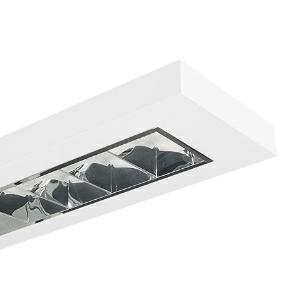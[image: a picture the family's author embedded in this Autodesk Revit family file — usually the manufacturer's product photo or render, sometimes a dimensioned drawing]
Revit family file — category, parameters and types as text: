
# Revit family: 3f_filippi_-_3f_travetta_di_2mg_3f_filippi_-_11597_-_3f_trav__led_di_2x22w-940_dali_2mg_l1590_0594
name_source: partatom
category: Lighting Fixtures
units: mm (PartAtom-declared; Revit-internal decimal feet)

## family parameters
Cut with Voids When Loaded = No
Host = Face
Light Source = No
Part Type = Normal
Room Calculation Point = No
Round Connector Dimension = Use Diameter
Shared = No

## types (1)
- 3F Filippi - 3F Travetta DI 2MG (1 x LED, 4545 lm, 49 W, 4000 K)
    Apparent Load = 49 VA
    Approval mark = ENEC
    CIE Flux Codes = 61 98 100 85 100
    Color Rendering = 90
    Color Temperature = 4000 K
    Control Gear = Electronic transformer
    Default Elevation = 1800 mm
    Description = ILLUMINOTECHNICAL
Luminous efficiency 100% (DLOR 85%, ULOR 15%).
Initial luminous flux of the luminaire 4545 lm.
Symmetric direct-indirect distribution.
Installation Interdistance Transv.D = 2.02 x hu - Long.D = 1.27 x hu.
Average luminance <1000 cd/m² for radial angles >65°.
Tabular UGR (CIE 117 - 4H-8H; S=0.25H; 70/50/20): RUG 17.5 - 16.9.
Beam angle: 99° - 72°.
Luminous efficacy 93 lm/W.
Lifetime (L93/B10): 30000 h. (tq+25°C)
Lifetime (L90/B10): 50000 h. (tq+25°C)
Lifetime (L85/B10): 80000 h. (tq+25°C)
Lifetime (L80/B10): 100000 h. (tq+25°C)
Sudden decreased luminous flux after 50000 hours: 0% (C0).
Photobiological safety in compliance with IEC/TR 62778: RG0 risk exempt, (IEC 62471).
In compliance with IEC/EN 62722-2-1 - IEC/EN 62717 standards.

SOURCE
2 linear LED modules 22W/940.
Energy efficiency class (UE 2019/2020 - UE 2019/2015): E.
CIE 13.3 Colour rendering index: CRI >90 (R9 >50%).
IES TM-30 Fidelity Index: Rf = 92 Rg = 101.
CCT nominal colour temperature 4000 K.
Colour initial tolerance (MacAdam): SDCM 2.

MECHANICAL
Housing with squared shape in white painted galvannealed steel, with nonreflecting surface.
2MG parabolic louvre, high efficiency, in specular aluminium with superficial titanium-magnesium treatment, non-iridescent, with transverse blades closed at the top.
Prismatic flat diffuser in transparent methacrylate (PMMA), multilenticular, anti-glare, prismatic exterior, placed above louvre blades.
Film protective against dust and finger marks, adhesive, attached to louvre.
Upper holes closing film made of opal polycarbonate.
Luminaire with limited surface temperature. - D - (EN 60598-2-24)
Dimensions: 1590x190 mm, height 60 mm. Weight 5.015 kg.
IP20 protection degree.
Glow-wire test resistance 650°C.

ELECTRICAL
Halogen Free DALI-2 DATI (Parts 251, 252, 253), PUSH-DIM, electronic wiring 230V-50/60Hz, power factor 0.95 at full load, THD <25%, constant output current, SELV, class I, 1 driver, 1 DALI addresse.
Power of the luminaire 49 W.
CE - IEC 60598-1 - EN 60598-1.
SAFE FLICKER: PstLM=<1 and SVM=<0.4 (IEC TR 61547-1 and IEC TR 63158), to ensure a more comfortable and safe light.
Luminaire compliant with EN 60598-2-22 for power supply from a centralised emergency system CPSS (Central Power Supply System), not incorporated in the luminaire - high risk areas excluded. The default power and flux are 100% in AC and 15% in DC.
Ambient temperature from 0°C to +25°C.
Temperature class T6 max 85°C.
Relative humidity UR: <85%.

INSTALLATION
Suspended.
All accessories dedicated to this product are available on the Catalog and on our website www.3F-Filippi.com.

APPLICATIONS
In environments, even with reduced height, requiring a comfortable light.
In environments with VDTs, managerial offices and staterooms, public offices and schools.

LIGHT MANAGEMENT
Recommended minimum setting: 10%.
The luminaire, equipped with (DALI-2 DATI) driver, can be controlled manually with 3F Easy Dim technology or automatically/manually with wired or wireless DALI/D2D control systems.
The D2D driver guarantees interoperability with other devices with the same certification by making the following information available:
Device Data (Part 251), Energy Report (Part 252), Diagnosis & Maintenance (Part 253).
In electrical systems without a regulation system (manual or automatic) and DALI bus, a suitable jumper must be made on the DA-DA terminals of the appliance.

WARNING
Luminaire designed for disposal/recycling at end-of-life.
Replaceable (LED only) light source by a professional. Replaceable control gear by a professional.
    Height = 60 mm  [stored 0.19685 ft]
    Lamp = 1 x LED
    Lamp Light Flux = 4545 lm
    Lamp Power = 49 W
    Lamp count = 1
    Length = 1590 mm
    Lifetime = 50000 h
    Luminous efficacy = 93 lm/W
    Manufacturer = 3F Filippi
    ModVariant = No
    Model = 3F Filippi - 11597 - 3F Trav. LED DI 2x22W-940 DALI 2MG L1590
    Mounting Place = Ceiling
    Mounting Type = Pendant
    Number of Poles = 1
    OnlyDefault = Yes
    Power Factor = 1
    Product Name = 3F Filippi - 3F Travetta DI 2MG
    Product group = pendant luminaire
    ProductGroupID = 9
    Protection Class = Protection class I
    Protection Degree = IP 20
    RLX_Detail_Level = 1
    RLX_Emergency_Light_Flux = 0 lm
    RLX_Emergency_Type = 0
    RLX_Emergency_Type_DB = No
    RlxData = <blob elided: 53445 chars, md5=e4803f16>
    Socket = socket
    Standby Power = 0 W
    System Light Flux = 4545 lm
    System Power = 49 W
    Type Comments = Product without accessories
    Type Image = 3ffilippi_3f_travetta_led_2mg.jpg
    URL = http://relux.com
    VarID = ---
    Voltage = 0 V
    Weight = 0.00 kg
    Width = 190 mm  [stored 0.62336 ft]

note: [stored X ft] marks values corroborated as IEEE doubles in the binary element streams (Revit-internal decimal feet)

## geometry (parser evidence)
native form markers: Blend x4, Sweep x13
no freeform markers — native parametric forms only
